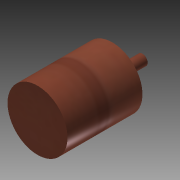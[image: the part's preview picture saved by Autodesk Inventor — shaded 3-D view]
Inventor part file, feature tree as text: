
AUTODESK INVENTOR PART (.ipt)
format: ipt  version: 2014 (Build 180170000, 170)  size: 92,160 bytes
history: native  units: mm
features: extrude x2, sketch x2, plane x1
ambient origin geometry x8: Origin, YZ Plane, XZ Plane, XY Plane, X Axis, Y Axis, Z Axis, Center Point
bodies: Solid1 (feature_tree)
feature tree (5):
  extrude  "Extrusion1"  Depth=50.0mm TaperAngle=0.0deg
  extrude  "Extrusion2"  Depth=20.0mm TaperAngle=0.0deg
  plane  "Work Plane1"
  sketch  "Sketch1"  dims[d0=40.0mm d1=50.0mm d2=0.0mm]
  sketch  "Sketch2"  dims[d3=7.0mm d4=20.0mm d5=0.0mm]
